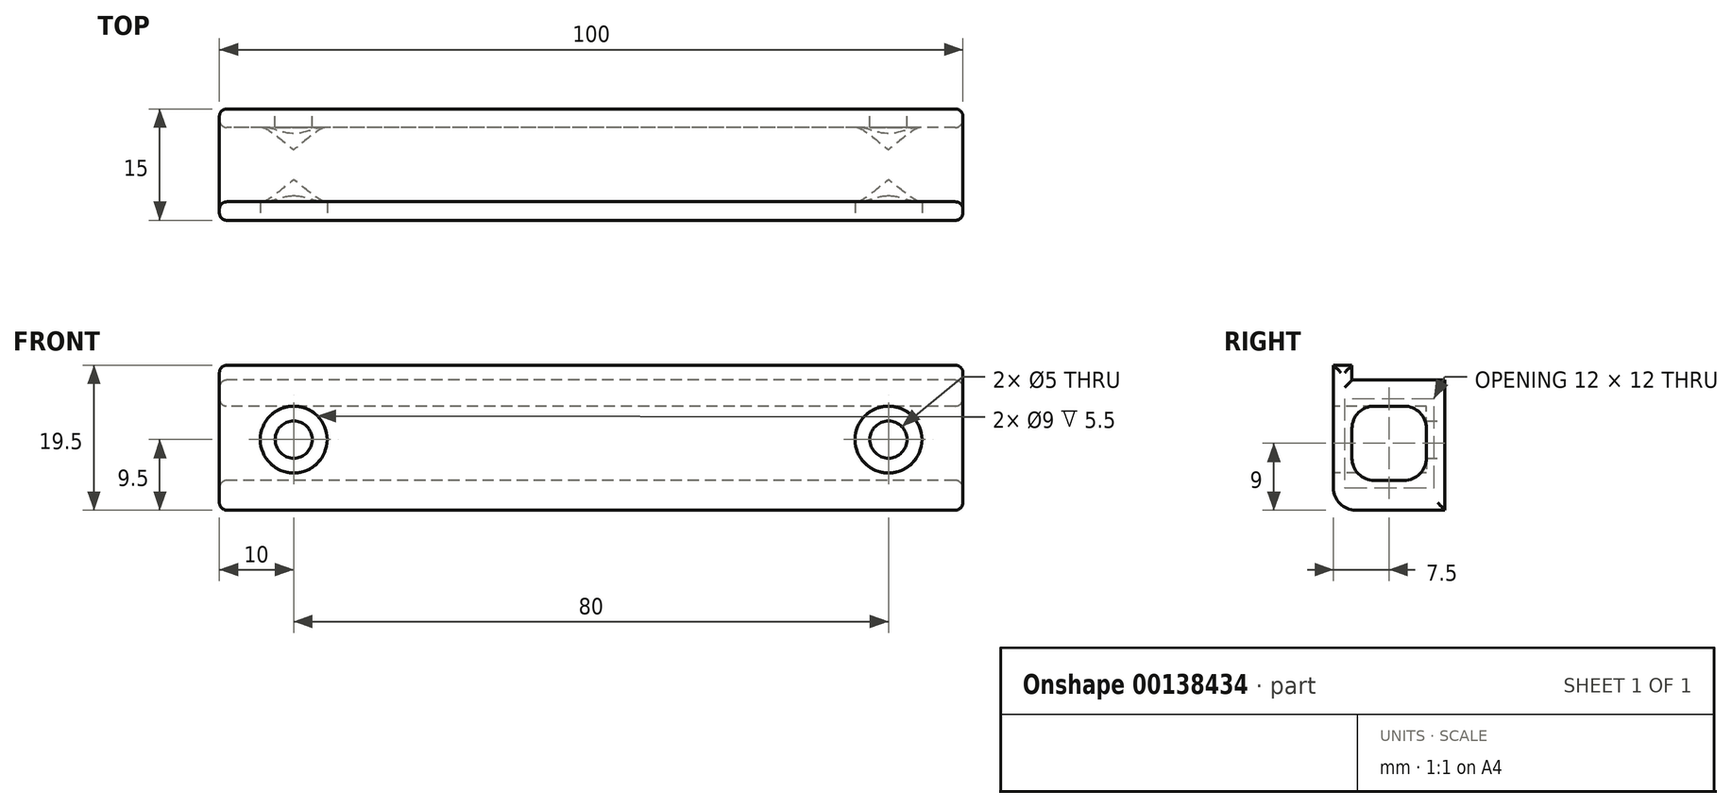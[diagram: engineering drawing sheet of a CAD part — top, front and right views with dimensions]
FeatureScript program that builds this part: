
annotation { "Feature Type Name" : "Feature", "Feature Type Description" : "" }
export const myFeature = defineFeature(function(context is Context, id is Id, definition is map)
    precondition{}
    {
        {
            var Q0;
            Q0=qCreatedBy(makeId("Right.planeOp"),FACE);
            var sketch = newSketch(context, id + "F0", { "sketchPlane" : qUnion([Q0])});
            skLineSegment(sketch, "E0", {"start": v(0, 0) * mm, "end": v(-15, 0) * mm});
            skLineSegment(sketch, "E1", {"start": v(-15, 0) * mm, "end": v(-15, 19.5) * mm});
            skLineSegment(sketch, "E2", {"start": v(-15, 19.5) * mm, "end": v(-12.5, 19.5) * mm});
            skLineSegment(sketch, "E3", {"start": v(-12.5, 19.5) * mm, "end": v(-12.5, 17.5) * mm});
            skLineSegment(sketch, "E4", {"start": v(-12.5, 17.5) * mm, "end": v(0, 17.5) * mm});
            skLineSegment(sketch, "E5", {"start": v(0, 17.5) * mm, "end": v(0, 0) * mm});
            skLineSegment(sketch, "E6.bottom", {"start": v(-9.5, 14) * mm, "end": v(-5.5, 14) * mm});
            skLineSegment(sketch, "E6.top", {"start": v(-9.5, 4) * mm, "end": v(-5.5, 4) * mm});
            skLineSegment(sketch, "E6.left", {"start": v(-12.5, 11) * mm, "end": v(-12.5, 7) * mm});
            skLineSegment(sketch, "E6.right", {"start": v(-2.5, 11) * mm, "end": v(-2.5, 7) * mm});
            skPoint(sketch, "E7.visualSharp", {"position": v(-12.5, 14) * mm});
            skArc(sketch, "E7.filletArc", {"start": v(-9.5, 14) * mm, "mid": v(-11.62, 13.12) * mm, "end": v(-12.5, 11) * mm});
            skPoint(sketch, "E8.visualSharp", {"position": v(-2.5, 14) * mm});
            skArc(sketch, "E8.filletArc", {"start": v(-2.5, 11) * mm, "mid": v(-3.38, 13.12) * mm, "end": v(-5.5, 14) * mm});
            skPoint(sketch, "E9.visualSharp", {"position": v(-2.5, 4) * mm});
            skArc(sketch, "E9.filletArc", {"start": v(-5.5, 4) * mm, "mid": v(-3.38, 4.88) * mm, "end": v(-2.5, 7) * mm});
            skPoint(sketch, "E10.visualSharp", {"position": v(-12.5, 4) * mm});
            skArc(sketch, "E10.filletArc", {"start": v(-12.5, 7) * mm, "mid": v(-11.62, 4.88) * mm, "end": v(-9.5, 4) * mm});
            skSolve(sketch);
        }
        {
            var Q0;
            Q0 = qSketchRegion(id + "F0", true);
            extrude(context, id + "F1", {"entities" : qUnion([Q0]), "depth" : 100 * mm});
        }
        {
            var Q0;
            Q0=makeQuery(id+"F1.opExtrude","SWEPT_EDGE",EDGE,{"disambiguationData":[OSD([sQuery(id+"F0.wireOp",EDGE,"E0"),sQuery(id+"F0.wireOp",EDGE,"E1")])]});
            fillet(context, id + "F2", {"entities" : qUnion([Q0]), "radius" : 3 * mm, "tangentPropagation" : true, "allowEdgeOverflow" : false});
        }
        {
            var Q0;
            Q0=makeQuery(id+"F1.opExtrude","CAP_FACE",FACE,{"disambiguationData":[OSD([sQuery(id+"F0.wireOp",EDGE,"E0"),sQuery(id+"F0.wireOp",EDGE,"E1"),sQuery(id+"F0.wireOp",EDGE,"E2"),sQuery(id+"F0.wireOp",EDGE,"E3"),sQuery(id+"F0.wireOp",EDGE,"E4"),sQuery(id+"F0.wireOp",EDGE,"E5"),sQuery(id+"F0.wireOp",EDGE,"E6.bottom"),sQuery(id+"F0.wireOp",EDGE,"E6.top"),sQuery(id+"F0.wireOp",EDGE,"E6.left"),sQuery(id+"F0.wireOp",EDGE,"E6.right"),sQuery(id+"F0.wireOp",EDGE,"E7.filletArc"),sQuery(id+"F0.wireOp",EDGE,"E8.filletArc"),sQuery(id+"F0.wireOp",EDGE,"E9.filletArc"),sQuery(id+"F0.wireOp",EDGE,"E10.filletArc")])],"isStart":false});
            var Q1;
            Q1=makeQuery(id+"F1.opExtrude","CAP_FACE",FACE,{"disambiguationData":[OSD([sQuery(id+"F0.wireOp",EDGE,"E0"),sQuery(id+"F0.wireOp",EDGE,"E1"),sQuery(id+"F0.wireOp",EDGE,"E2"),sQuery(id+"F0.wireOp",EDGE,"E3"),sQuery(id+"F0.wireOp",EDGE,"E4"),sQuery(id+"F0.wireOp",EDGE,"E5"),sQuery(id+"F0.wireOp",EDGE,"E6.bottom"),sQuery(id+"F0.wireOp",EDGE,"E6.top"),sQuery(id+"F0.wireOp",EDGE,"E6.left"),sQuery(id+"F0.wireOp",EDGE,"E6.right"),sQuery(id+"F0.wireOp",EDGE,"E7.filletArc"),sQuery(id+"F0.wireOp",EDGE,"E8.filletArc"),sQuery(id+"F0.wireOp",EDGE,"E9.filletArc"),sQuery(id+"F0.wireOp",EDGE,"E10.filletArc")])],"isStart":true});
            fillet(context, id + "F3", {"entities" : qUnion([Q0, Q1]), "radius" : 1 * mm, "tangentPropagation" : true, "allowEdgeOverflow" : false});
        }
        {
            var Q0;
            Q0=makeQuery(id+"F1.opExtrude","SWEPT_FACE",FACE,{"disambiguationData":[OSD([sQuery(id+"F0.wireOp",EDGE,"E5")])]});
            var sketch = newSketch(context, id + "F4", { "sketchPlane" : qUnion([Q0])});
            skCircle(sketch, "E11", {"center": v(-90, 9.5) * mm, "radius": 2.5 * mm});
            skCircle(sketch, "E12", {"center": v(-10, 9.5) * mm, "radius": 2.5 * mm});
            skSolve(sketch);
        }
        {
            var Q0;
            Q0 = qSketchRegion(id + "F4", true);
            extrude(context, id + "F5", {"entities" : qUnion([Q0]), "operationType" : NewBodyOperationType.REMOVE, "oppositeDirection" : true, "depth" : 25 * mm});
        }
        {
            var Q0;
            Q0=makeQuery(id+"F1.opExtrude","SWEPT_FACE",FACE,{"disambiguationData":[OSD([sQuery(id+"F0.wireOp",EDGE,"E1")])]});
            var sketch = newSketch(context, id + "F6", { "sketchPlane" : qUnion([Q0])});
            skCircle(sketch, "E13", {"center": v(10, 9.5) * mm, "radius": 4.5 * mm});
            skCircle(sketch, "E14", {"center": v(90, 9.5) * mm, "radius": 4.5 * mm});
            skSolve(sketch);
        }
        {
            var Q0;
            Q0 = qSketchRegion(id + "F6", true);
            var Q1;
            Q1=makeQuery(id+"F1.opExtrude","SWEPT_FACE",FACE,{"disambiguationData":[OSD([sQuery(id+"F0.wireOp",EDGE,"E6.left")])]});
            var Q2;
            Q2=makeQuery(id+"F1.opExtrude","SWEPT_FACE",FACE,{"disambiguationData":[OSD([sQuery(id+"F0.wireOp",EDGE,"E6.right")])]});
            extrude(context, id + "F7", {"entities" : qUnion([Q0, Q1]), "operationType" : NewBodyOperationType.REMOVE, "endBound" : BoundingType.UP_TO_SURFACE, "oppositeDirection" : true, "endBoundEntityFace" : qUnion([Q2]), "depth" : 5 * mm});
        }
    });
